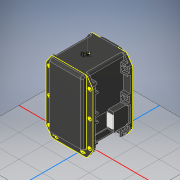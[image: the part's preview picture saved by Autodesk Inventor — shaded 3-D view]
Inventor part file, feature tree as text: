
AUTODESK INVENTOR PART (.ipt)
format: ipt  version: 2022 (Build 260153000, 153)  size: 559,104 bytes
history: native  units: mm
features: sketch x4, projected_geometry x3, extrude x1, other x1, imported_body x1
ambient origin geometry x8: Origin, YZ Plane, XZ Plane, XY Plane, X Axis, Y Axis, Z Axis, Center Point
bodies: Solid1 (feature_tree)
feature tree (10):
  extrude  "Extrusion1"  Depth=10.0mm
  sketch  "Эскиз2"
  sketch  "Эскиз3"
  sketch  "Эскиз4"
  other  "РабОсь1"
  sketch  "Sketch1"  dims[d0=10.0mm d1=0.0mm d2=0.9mm]
  projected_geometry  "Projected Loop1"
  projected_geometry  "Спроецированная петля2"
  projected_geometry  "Спроецированная петля3"
  imported_body  "Base1"
